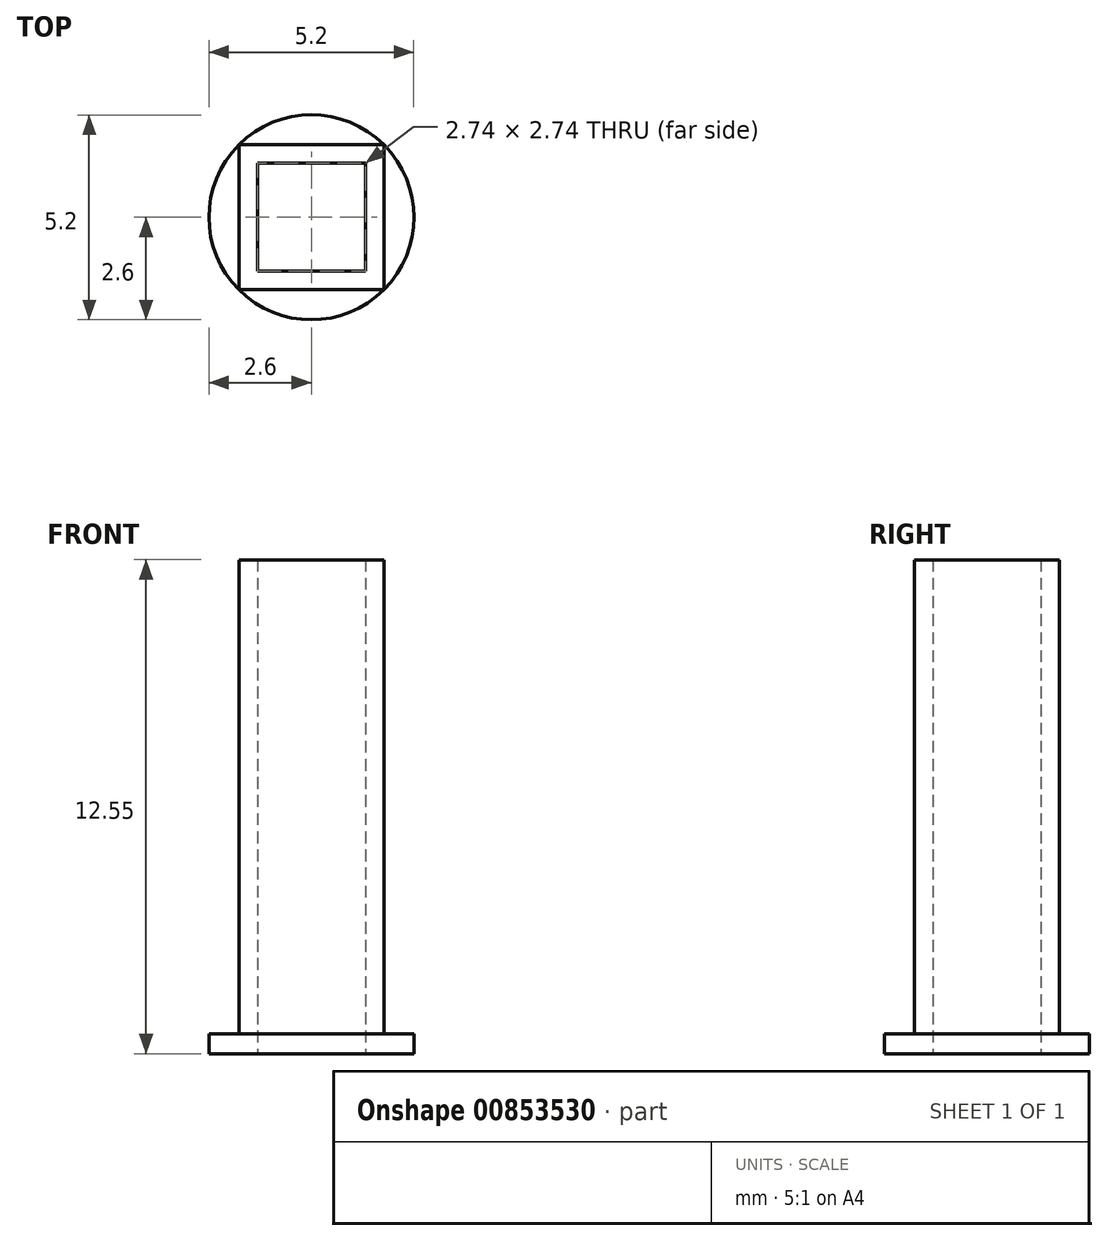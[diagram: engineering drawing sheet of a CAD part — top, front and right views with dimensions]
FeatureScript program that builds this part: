
annotation { "Feature Type Name" : "Feature", "Feature Type Description" : "" }
export const myFeature = defineFeature(function(context is Context, id is Id, definition is map)
    precondition{}
    {
        {
            var Q0;
            Q0=qCreatedBy(makeId("Top.planeOp"),FACE);
            var sketch = newSketch(context, id + "F0", { "sketchPlane" : qUnion([Q0])});
            skCircle(sketch, "E0", {"center": v(0, 0) * mm, "radius": 2.6 * mm});
            skLineSegment(sketch, "E1.bottom", {"start": v(1.37, 1.37) * mm, "end": v(-1.37, 1.37) * mm});
            skLineSegment(sketch, "E1.top", {"start": v(1.37, -1.37) * mm, "end": v(-1.37, -1.37) * mm});
            skLineSegment(sketch, "E1.left", {"start": v(1.37, 1.37) * mm, "end": v(1.37, -1.37) * mm});
            skLineSegment(sketch, "E1.right", {"start": v(-1.37, 1.37) * mm, "end": v(-1.37, -1.37) * mm});
            skSolve(sketch);
        }
        {
            var Q0;
            Q0=makeQuery(id+"F0.imprint","IMPRINT",FACE,{"disambiguationData":[TD([[makeQuery(id+"F0.imprint","IMPRINT",EDGE,{"derivedFrom":sQuery(id+"F0.wireOp",EDGE,"E0")}),1.0]])]});
            extrude(context, id + "F1", {"entities" : qUnion([Q0]), "depth" : 0.5 * mm, "offsetDistance" : 25.4 * mm});
        }
        {
            var Q0;
            Q0=makeQuery(id+"F1.opExtrude","CAP_FACE",FACE,{"disambiguationData":[OSD([sQuery(id+"F0.wireOp",EDGE,"E0"),sQuery(id+"F0.wireOp",EDGE,"E1.bottom"),sQuery(id+"F0.wireOp",EDGE,"E1.top"),sQuery(id+"F0.wireOp",EDGE,"E1.left"),sQuery(id+"F0.wireOp",EDGE,"E1.right")])],"isStart":false});
            var sketch = newSketch(context, id + "F2", { "sketchPlane" : qUnion([Q0])});
            skLineSegment(sketch, "E2.bottom", {"start": v(1.84, 1.84) * mm, "end": v(-1.84, 1.84) * mm});
            skLineSegment(sketch, "E2.top", {"start": v(1.84, -1.84) * mm, "end": v(-1.84, -1.84) * mm});
            skLineSegment(sketch, "E2.left", {"start": v(1.84, 1.84) * mm, "end": v(1.84, -1.84) * mm});
            skLineSegment(sketch, "E2.right", {"start": v(-1.84, 1.84) * mm, "end": v(-1.84, -1.84) * mm});
            skPoint(sketch, "E2.middle", {"position": v(0, 0) * mm});
            skLineSegment(sketch, "E3.0", {"start": v(1.37, 1.37) * mm, "end": v(-1.37, 1.37) * mm});
            skLineSegment(sketch, "E4.0", {"start": v(-1.37, 1.37) * mm, "end": v(-1.37, -1.37) * mm});
            skLineSegment(sketch, "E5.0", {"start": v(1.37, -1.37) * mm, "end": v(-1.37, -1.37) * mm});
            skPoint(sketch, "E6.0", {"position": v(1.37, 0) * mm});
            skLineSegment(sketch, "E7.0", {"start": v(1.37, 1.37) * mm, "end": v(1.37, -1.37) * mm});
            skSolve(sketch);
        }
        {
            var Q0;
            Q0 = qSketchRegion(id + "F2", true);
            extrude(context, id + "F3", {"entities" : qUnion([Q0]), "operationType" : NewBodyOperationType.ADD, "depth" : 12.04 * mm, "offsetDistance" : 25.4 * mm});
        }
    });
